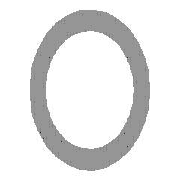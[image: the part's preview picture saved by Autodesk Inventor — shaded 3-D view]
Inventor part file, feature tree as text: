
AUTODESK INVENTOR PART (.ipt)
format: ipt  version: 2017 (Build 210142000, 142)  size: 117,248 bytes
history: native  units: mm (DEFAULTED — no unit token found)
features: other x4, sketch x3, plane x1
ambient origin geometry x8: Origin, YZ Plane, XZ Plane, XY Plane, X Axis, Y Axis, Z Axis, Center Point
bodies: Solid1 (feature_tree), Body (feature_tree)
feature tree (8):
  other  "Tubular Redondo - 25x1,5 - 970mm"
  other  "Driven Length"
  other  "Start plane"
  other  "End plane"
  sketch  "Sketch"  dims[d2=1010.0mm d3=0.0mm d4=-0.0mm d5=1010.0mm d6=90.0deg d7=1010.0mm]
  sketch  "Sketch3"  dims[d0=25.0mm]
  plane  "Work Plane3"
  sketch  "Sketch4"  dims[d1=1.5mm]
